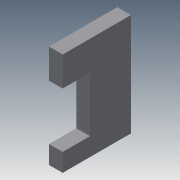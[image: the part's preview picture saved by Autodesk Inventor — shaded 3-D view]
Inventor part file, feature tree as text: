
AUTODESK INVENTOR PART (.ipt)
format: ipt  version: 2013 (Build 170138000, 138)  size: 446,464 bytes
history: native  units: mm
features: extrude x34, sketch x34, fillet x1
ambient origin geometry x8: Origin, YZ Plane, XZ Plane, XY Plane, X Axis, Y Axis, Z Axis, Center Point
bodies: Solid1 (feature_tree)
feature tree (69):
  extrude  "Extrusion1"  Depth=6.0mm
  extrude  "Extrusion2"  Depth=24.3mm
  extrude  "Extrusion3"  Depth=24.3mm
  extrude  "Extrusion4"  Depth=10.0mm
  sketch  "Sketch5"  dims[d9=60.0mm d10=60.0mm]
  extrude  "Extrusion5"  Depth=60.0mm
  extrude  "Extrusion6"  Depth=15.0mm
  extrude  "Extrusion7"  Depth=15.0mm
  extrude  "Extrusion8"  Depth=3.0mm
  extrude  "Extrusion9"  Depth=3.0mm
  extrude  "Extrusion10"  Depth=71.2mm
  extrude  "Extrusion11"  Depth=55.0mm
  extrude  "Extrusion12"  Depth=10.0mm
  extrude  "Extrusion13"  Depth=5.0mm TaperAngle=0.0deg
  extrude  "Extrusion15"  Depth=4.0mm
  extrude  "Extrusion16"  Depth=48.0mm TaperAngle=0.0deg
  extrude  "Extrusion17"  Depth=34.25mm
  extrude  "Extrusion22"  Depth=40.2mm
  sketch  "Sketch24"  dims[d55=49.7mm d56=40.2mm]
  sketch  "Sketch25"  dims[d60=3.0mm d61=3.0mm]
  extrude  "Extrusion23"  Depth=3.0mm
  extrude  "Extrusion24"  Depth=3.0mm
  sketch  "Sketch29"  dims[d64=10.0mm d65=0.0mm d66=3.0mm d67=0.0mm]
  extrude  "Extrusion28"  Depth=3.0mm TaperAngle=0.0deg
  extrude  "Extrusion29"  Depth=4.0mm
  extrude  "Extrusion30"  Depth=8.0mm
  extrude  "Extrusion31"  Depth=15.0mm
  extrude  "Extrusion32"  Depth=6.0mm TaperAngle=0.0deg
  extrude  "Extrusion33"  Depth=14.3mm
  extrude  "Extrusion34"  Depth=48.6mm
  extrude  "Extrusion35"  Depth=35.0mm
  fillet  "Fillet9"  Radius=14.3mm
  extrude  "Extrusion36"  Depth=24.0mm TaperAngle=0.0deg
  extrude  "Extrusion37"  Depth=4.589mm
  sketch  "Sketch41"  dims[d102=4.589mm d103=10.0mm d104=0.0mm]
  extrude  "Extrusion38"  Depth=19.125mm
  extrude  "Extrusion39"  Depth=10.0mm TaperAngle=0.0deg
  extrude  "Extrusion40"  Depth=10.0mm TaperAngle=0.0deg
  extrude  "Extrusion41"  Depth=2.0mm TaperAngle=0.0deg
  extrude  "Extrusion42"  Depth=2.0mm TaperAngle=0.0deg
  sketch  "Sketch1"  dims[d0=120.0mm d1=6.0mm]
  sketch  "Sketch2"  dims[d2=10.0mm d3=0.0mm d4=24.3mm]
  sketch  "Sketch3"  dims[d5=5.0mm d6=24.3mm]
  sketch  "Sketch4"  dims[d7=5.0mm d8=10.0mm]
  sketch  "Sketch6"  dims[d11=15.0mm d12=15.0mm]
  sketch  "Sketch7"  dims[d13=15.0mm d14=15.0mm]
  sketch  "Sketch8"  dims[d15=3.0mm d16=3.0mm]
  sketch  "Sketch9"  dims[d17=3.0mm d18=3.0mm]
  sketch  "Sketch10"  dims[d19=10.0mm d20=0.0mm d31=71.2mm]
  sketch  "Sketch11"  dims[d32=34.25mm d33=55.0mm]
  sketch  "Sketch12"  dims[d34=10.0mm d35=0.0mm d36=10.0mm]
  sketch  "Sketch14"  dims[d37=43.0mm d38=0.0mm d41=5.0mm d42=0.0mm]
  sketch  "Sketch16"  dims[d45=4.0mm d46=4.0mm]
  sketch  "Sketch18"  dims[d47=10.0mm d48=0.0mm d49=48.0mm d50=0.0mm]
  sketch  "Sketch23"  dims[d51=35.0mm d54=34.25mm]
  sketch  "Sketch26"  dims[d62=3.0mm d63=3.0mm]
  sketch  "Sketch31"  dims[d70=14.209mm d71=4.0mm]
  sketch  "Sketch32"  dims[d72=10.0mm d73=0.0mm d74=8.0mm]
  sketch  "Sketch33"  dims[d75=10.0mm d76=0.0mm d78=15.0mm]
  sketch  "Sketch34"  dims[d79=10.0mm d80=6.0mm d81=0.0mm]
  sketch  "Sketch35"  dims[d82=14.3mm d83=14.3mm]
  sketch  "Sketch36"  dims[d84=6.0mm d85=0.0mm d90=48.6mm]
  sketch  "Sketch37"  dims[d91=14.3mm d92=35.0mm d93=14.3mm]
  sketch  "Sketch38"  dims[d94=35.0mm d95=24.0mm d96=0.0mm]
  sketch  "Sketch39"  dims[d97=19.125mm d98=4.589mm]
  sketch  "Sketch40"  dims[d99=10.0mm d100=0.0mm d101=19.125mm]
  sketch  "Sketch42"  dims[d123=15.0mm d124=10.0mm d125=0.0mm]
  sketch  "Sketch43"  dims[d126=35.0mm d129=2.0mm d130=0.0mm]
  sketch  "Sketch44"  dims[d131=10.0mm d132=2.0mm d133=0.0mm d144=7.5mm d145=10.0mm d146=0.0mm d147=3.0mm d148=6.0mm d149=2.0mm d150=10.0mm d151=0.0mm d152=24.0mm d153=0.0mm d154=24.0mm d155=0.0mm d156=6.0mm d157=0.0mm d158=15.0mm d159=24.0mm d160=6.0mm d161=0.0mm d162=16.0mm d163=20.0mm d164=6.0mm d165=0.0mm d166=17.0mm d167=6.0mm d168=0.0mm d169=2.0mm d170=2.0mm d171=0.0mm d172=10.0mm d173=0.0mm d174=10.0mm d175=0.0mm d176=10.0mm d177=0.0mm d178=37.5mm d179=75.0mm d180=10.0mm d181=0.0mm d182=5.0mm d183=0.0mm d184=0.1mm d185=0.1mm d186=0.1mm d187=0.1mm d188=10.0mm d189=0.0mm]
